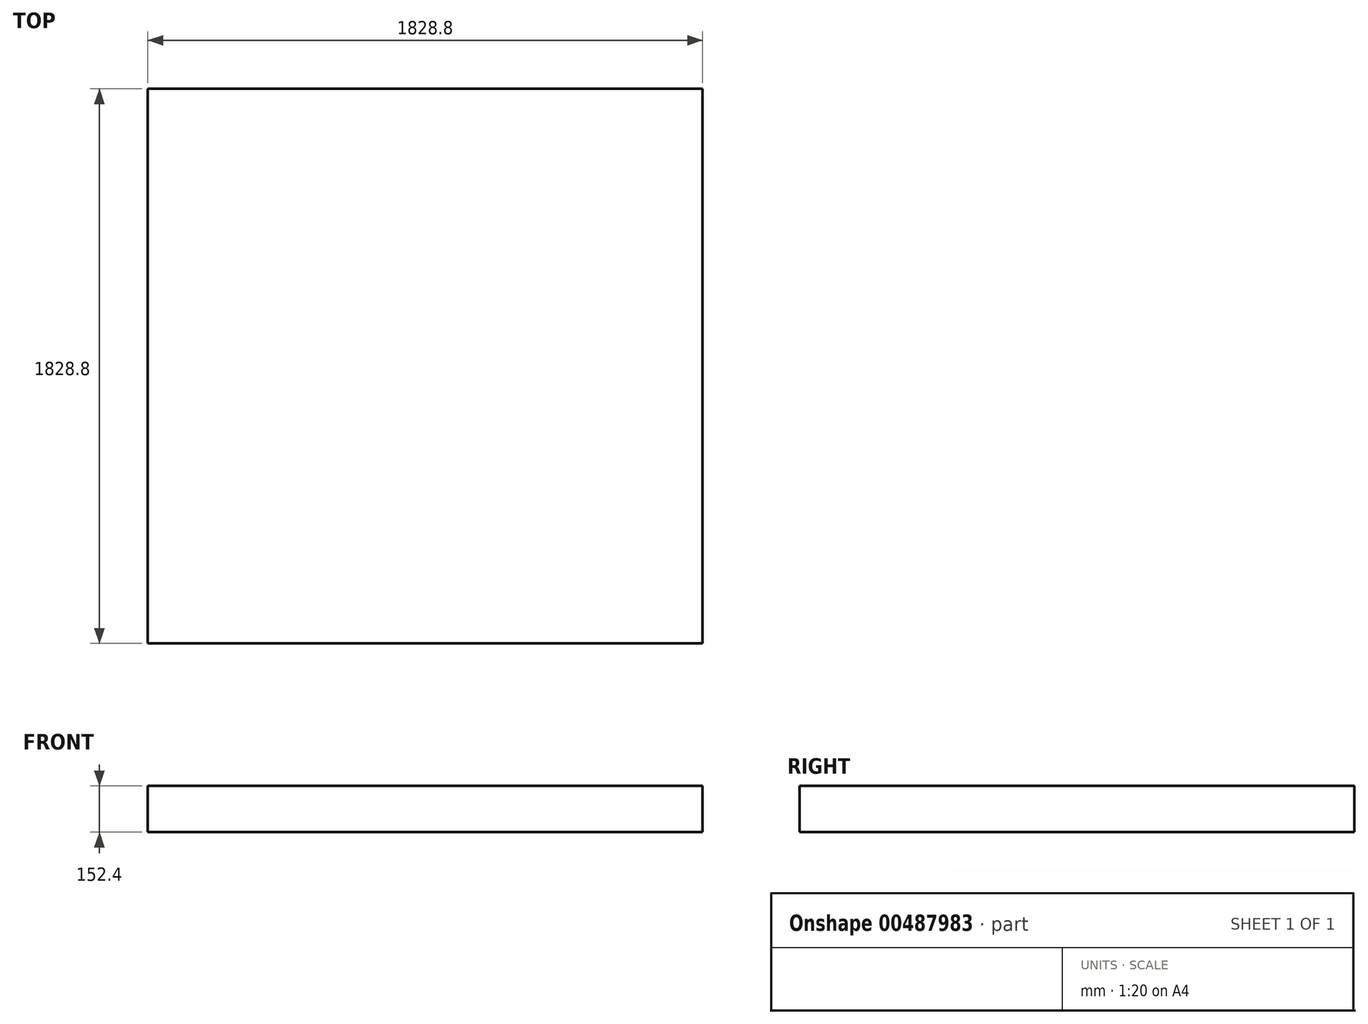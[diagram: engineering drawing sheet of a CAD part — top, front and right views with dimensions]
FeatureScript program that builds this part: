
annotation { "Feature Type Name" : "Feature", "Feature Type Description" : "" }
export const myFeature = defineFeature(function(context is Context, id is Id, definition is map)
    precondition{}
    {
        {
            var Q0;
            Q0=qCreatedBy(makeId("Front.planeOp"),FACE);
            var sketch = newSketch(context, id + "F0", { "sketchPlane" : qUnion([Q0])});
            skLineSegment(sketch, "E0.bottom", {"start": v(-914.4, 0) * mm, "end": v(914.4, 0) * mm});
            skLineSegment(sketch, "E0.top", {"start": v(-914.4, 152.4) * mm, "end": v(914.4, 152.4) * mm});
            skLineSegment(sketch, "E0.left", {"start": v(-914.4, 0) * mm, "end": v(-914.4, 152.4) * mm});
            skLineSegment(sketch, "E0.right", {"start": v(914.4, 0) * mm, "end": v(914.4, 152.4) * mm});
            skSolve(sketch);
        }
        {
            var Q0;
            Q0 = qSketchRegion(id + "F0", true);
            extrude(context, id + "F1", {"entities" : qUnion([Q0]), "endBound" : BoundingType.SYMMETRIC, "depth" : 1828.8 * mm});
        }
    });
